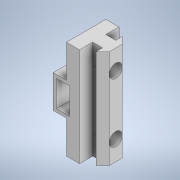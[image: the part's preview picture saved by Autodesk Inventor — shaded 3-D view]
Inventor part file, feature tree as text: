
AUTODESK INVENTOR PART (.ipt)
format: ipt  version: 2020 (Build 240168000, 168)  size: 168,448 bytes
history: native  units: in
note: dims shown in document units (in); Inventor stores cm internally (conversion verified against a paired STEP export)
features: sketch x4, extrude x3, other x2, hole x1
ambient origin geometry x8: Origin, YZ Plane, XZ Plane, XY Plane, X Axis, Y Axis, Z Axis, Center Point
bodies: Solid1 (feature_tree)
feature tree (10):
  other  "Annotations"
  extrude  "Extrusion1"  Depth=0.6in
  hole  "Hole1"  [1 undecoded]
  extrude  "Extrusion2"  Depth=0.1in
  extrude  "Extrusion3"  Depth=0.1in
  sketch  "Sketch1"  dims[d0=0.2in d1=0.6in]
  sketch  "Sketch2"  dims[d2=0.1in d3=0.15in]
  sketch  "Sketch3"  dims[d4=0.1in d5=0.1in]
  sketch  "Sketch4"  dims[d6=0.2in d7=0.1in d8=1.5in d9=0.0in d10=0.3in d11=0.3in d12=0.2in d13=0.75in d14=0.4in d15=0.15in d16=0.5635in d17=1.0in d18=0.8108in d19=0.5in d20=0.5in d21=0.2in d22=0.0in d23=0.05in d24=0.05in d25=0.2in d26=0.4in d27=0.6in d28=0.0in d29=0.1606in d30=0.1409in d31=0.05in]
  other  "Linear Dimension 1"
note: 1 required parameter value undecoded (feature->parameter linkage not recoverable at this tier; creation-order binding heuristic only, values carry confidence <= 0.55)
